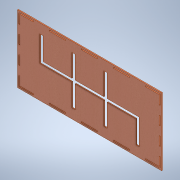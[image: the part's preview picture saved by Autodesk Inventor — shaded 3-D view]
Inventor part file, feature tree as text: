
AUTODESK INVENTOR PART (.ipt)
format: ipt  version: 2020.3 (Build 243373000, 373)  size: 243,712 bytes
history: native  units: mm
features: other x1, extrude x1, sketch x1
ambient origin geometry x8: Origin, YZ Plane, XZ Plane, XY Plane, X Axis, Y Axis, Z Axis, Center Point
bodies: Body1 (feature_tree)
feature tree (3):
  other  "Sólido1"
  extrude  "Extrusión1"  Depth=450.0mm
  sketch  "Boceto1"  dims[d91=3.0mm d92=0.0mm d93=450.0mm d94=210.0mm d95=210.0mm d96=450.0mm d97=5.0mm d98=30.71mm d99=45.0mm d100=5.0mm d101=3.0mm d102=3.0mm d103=5.0mm d104=5.0mm d105=3.0mm d106=30.71mm d107=45.0mm d108=3.0mm d109=5.0mm d110=30.71mm d111=45.0mm d112=5.0mm d113=3.0mm d114=3.0mm d115=30.71mm d116=5.0mm d117=45.0mm d118=5.0mm d119=3.0mm d120=3.0mm d121=3.0mm d122=3.0mm d123=3.0mm d124=5.0mm d125=5.0mm d126=5.0mm d127=5.0mm d128=5.0mm d129=5.0mm d130=27.72mm d131=27.71mm d132=27.71mm d133=27.72mm d134=27.72mm d135=50.0mm d136=50.0mm d137=50.0mm d138=50.0mm d139=50.0mm d140=50.0mm d141=50.0mm]
